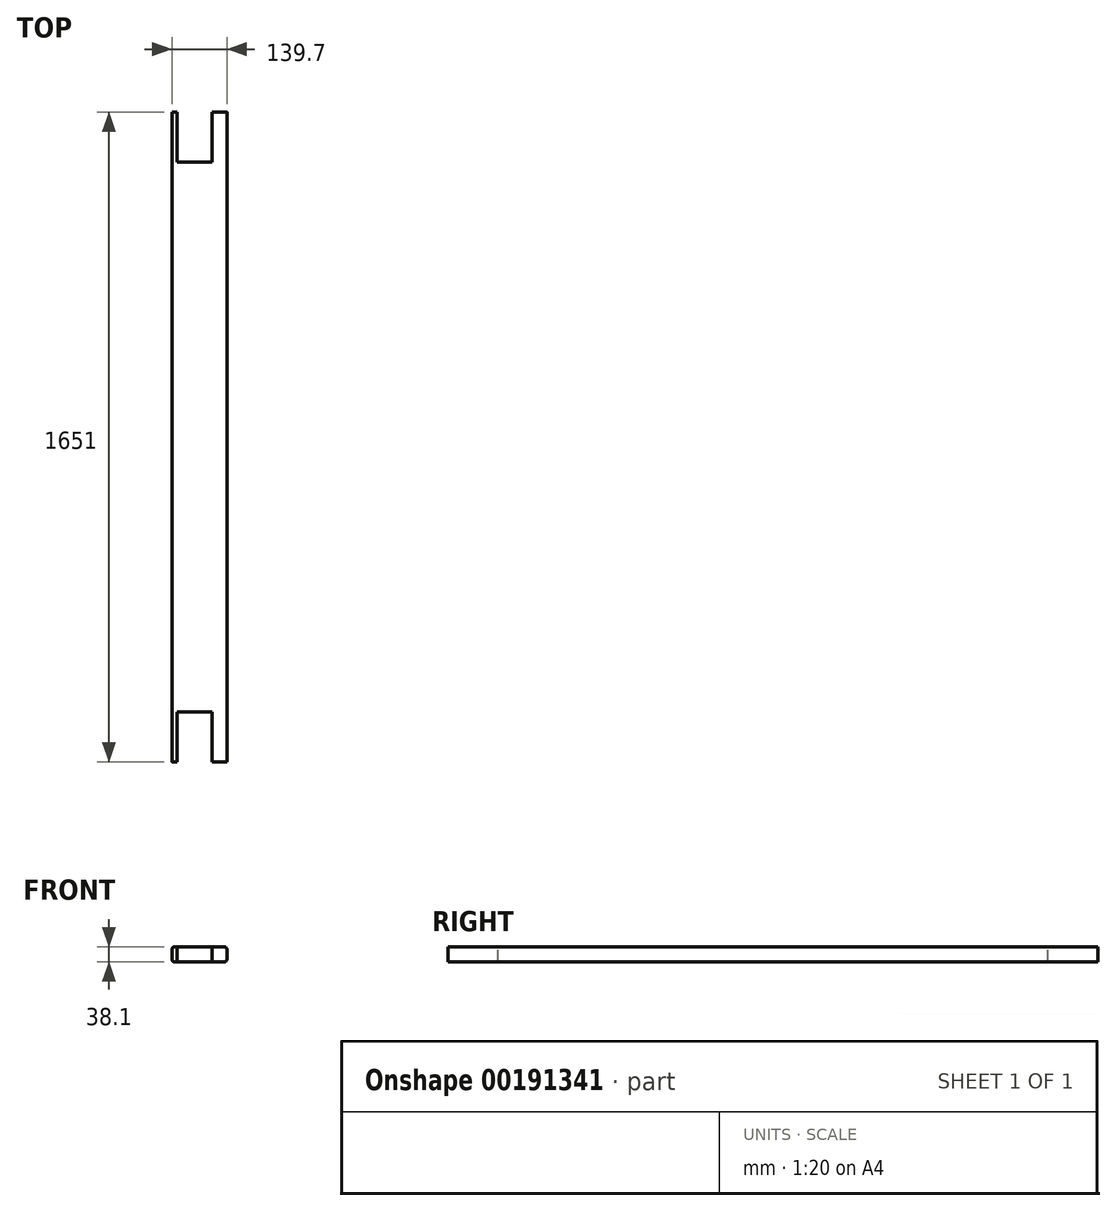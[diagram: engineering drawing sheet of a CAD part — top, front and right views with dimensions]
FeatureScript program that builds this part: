
annotation { "Feature Type Name" : "Feature", "Feature Type Description" : "" }
export const myFeature = defineFeature(function(context is Context, id is Id, definition is map)
    precondition{}
    {
        {
            var Q0;
            Q0=qCreatedBy(makeId("Front.planeOp"),FACE);
            var sketch = newSketch(context, id + "F0", { "sketchPlane" : qUnion([Q0])});
            skLineSegment(sketch, "E0.bottom", {"start": v(-63.5, -19.05) * mm, "end": v(63.5, -19.05) * mm});
            skLineSegment(sketch, "E0.top", {"start": v(-63.5, 19.05) * mm, "end": v(63.5, 19.05) * mm});
            skLineSegment(sketch, "E0.left", {"start": v(-69.85, -12.7) * mm, "end": v(-69.85, 12.7) * mm});
            skLineSegment(sketch, "E0.right", {"start": v(69.85, -12.7) * mm, "end": v(69.85, 12.7) * mm});
            skPoint(sketch, "E0.middle", {"position": v(0, 0) * mm});
            skPoint(sketch, "E1.visualSharp", {"position": v(-69.85, 19.05) * mm});
            skArc(sketch, "E1.filletArc", {"start": v(-63.5, 19.05) * mm, "mid": v(-68, 17.2) * mm, "end": v(-69.85, 12.7) * mm});
            skPoint(sketch, "E2.visualSharp", {"position": v(69.85, 19.05) * mm});
            skArc(sketch, "E2.filletArc", {"start": v(69.85, 12.7) * mm, "mid": v(68, 17.2) * mm, "end": v(63.5, 19.05) * mm});
            skPoint(sketch, "E3.visualSharp", {"position": v(69.85, -19.05) * mm});
            skArc(sketch, "E3.filletArc", {"start": v(63.5, -19.05) * mm, "mid": v(68, -17.2) * mm, "end": v(69.85, -12.7) * mm});
            skPoint(sketch, "E4.visualSharp", {"position": v(-69.85, -19.05) * mm});
            skArc(sketch, "E4.filletArc", {"start": v(-69.85, -12.7) * mm, "mid": v(-68, -17.2) * mm, "end": v(-63.5, -19.05) * mm});
            skSolve(sketch);
        }
        {
            var Q0;
            Q0 = qSketchRegion(id + "F0", true);
            extrude(context, id + "F1", {"entities" : qUnion([Q0]), "depth" : 1651 * mm});
        }
        {
            var Q0;
            Q0=makeQuery(id+"F1.opExtrude","SWEPT_FACE",FACE,{"disambiguationData":[OSD([sQuery(id+"F0.wireOp",EDGE,"E0.top")])]});
            var sketch = newSketch(context, id + "F2", { "sketchPlane" : qUnion([Q0])});
            skLineSegment(sketch, "E5.bottom", {"start": v(31.75, 0) * mm, "end": v(-57.15, 0) * mm});
            skLineSegment(sketch, "E5.top", {"start": v(31.75, -127) * mm, "end": v(-57.15, -127) * mm});
            skLineSegment(sketch, "E5.left", {"start": v(31.75, 0) * mm, "end": v(31.75, -127) * mm});
            skLineSegment(sketch, "E5.right", {"start": v(-57.15, 0) * mm, "end": v(-57.15, -127) * mm});
            skSolve(sketch);
        }
        {
            var Q0;
            Q0 = qSketchRegion(id + "F2", true);
            extrude(context, id + "F3", {"entities" : qUnion([Q0]), "operationType" : NewBodyOperationType.REMOVE, "endBound" : BoundingType.THROUGH_ALL, "oppositeDirection" : true, "depth" : 25.4 * mm});
        }
        {
            var Q0;
            Q0=makeQuery(id+"F1.opExtrude","SWEPT_FACE",FACE,{"disambiguationData":[OSD([sQuery(id+"F0.wireOp",EDGE,"E0.top")])]});
            var sketch = newSketch(context, id + "F4", { "sketchPlane" : qUnion([Q0])});
            skLineSegment(sketch, "E6.bottom", {"start": v(31.75, -1651) * mm, "end": v(-57.15, -1651) * mm});
            skLineSegment(sketch, "E6.top", {"start": v(31.75, -1524) * mm, "end": v(-57.15, -1524) * mm});
            skLineSegment(sketch, "E6.left", {"start": v(31.75, -1651) * mm, "end": v(31.75, -1524) * mm});
            skLineSegment(sketch, "E6.right", {"start": v(-57.15, -1651) * mm, "end": v(-57.15, -1524) * mm});
            skSolve(sketch);
        }
        {
            var Q0;
            Q0 = qSketchRegion(id + "F4", true);
            extrude(context, id + "F5", {"entities" : qUnion([Q0]), "operationType" : NewBodyOperationType.REMOVE, "endBound" : BoundingType.THROUGH_ALL, "oppositeDirection" : true, "depth" : 25.4 * mm});
        }
    });
